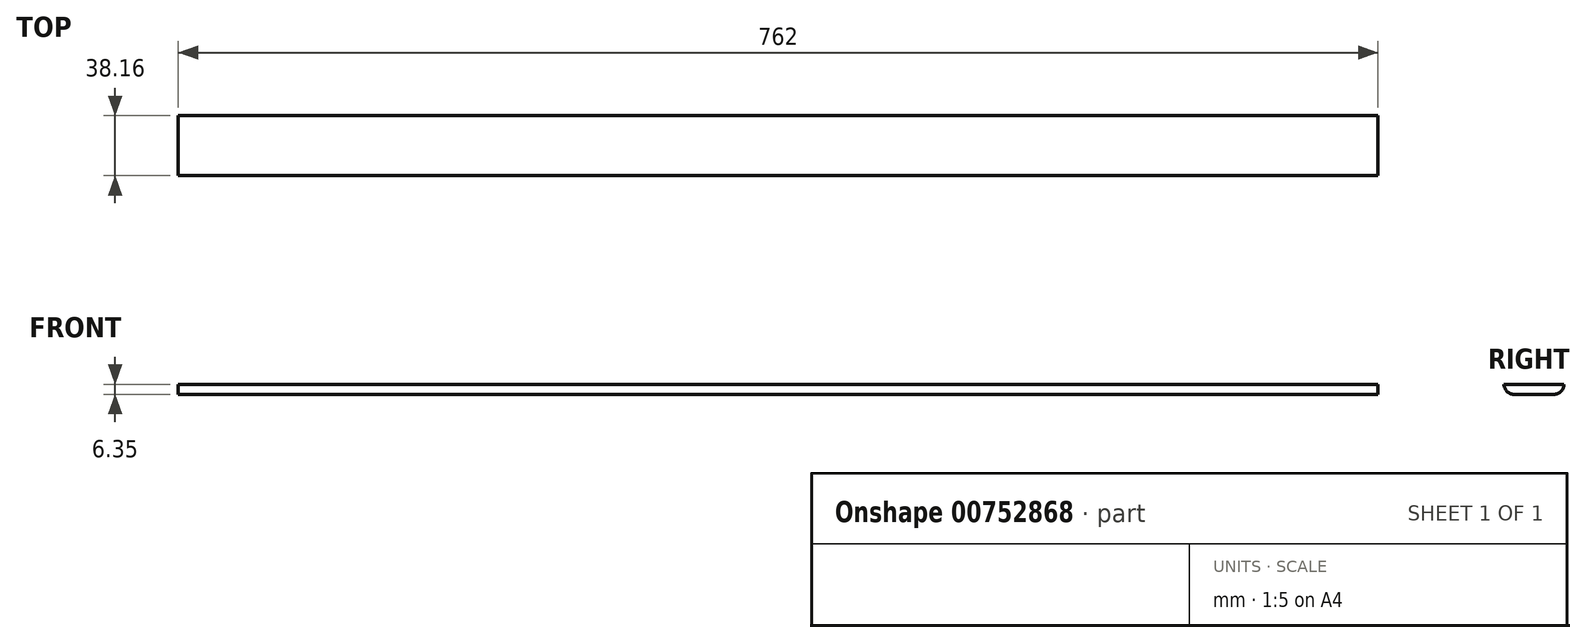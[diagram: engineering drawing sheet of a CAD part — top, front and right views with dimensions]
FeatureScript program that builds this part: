
annotation { "Feature Type Name" : "Feature", "Feature Type Description" : "" }
export const myFeature = defineFeature(function(context is Context, id is Id, definition is map)
    precondition{}
    {
        {
            var Q0;
            Q0=qCreatedBy(makeId("Right.planeOp"),FACE);
            var sketch = newSketch(context, id + "F0", { "sketchPlane" : qUnion([Q0])});
            skCircle(sketch, "E0", {"center": v(0, 2.7) * mm, "radius": 25 * mm});
            skCircle(sketch, "E1", {"center": v(0, 16.7) * mm, "radius": 11 * mm});
            skCircle(sketch, "E2", {"center": v(0, 16.7) * mm, "radius": 3.75 * mm});
            skLineSegment(sketch, "E3.bottom", {"start": v(12.73, 2.53) * mm, "end": v(-12.73, 2.53) * mm});
            skLineSegment(sketch, "E3.top", {"start": v(12.73, -10.17) * mm, "end": v(-12.73, -10.17) * mm});
            skLineSegment(sketch, "E3.left", {"start": v(19.08, -3.82) * mm, "end": v(19.08, -3.82) * mm});
            skLineSegment(sketch, "E3.right", {"start": v(-19.08, -3.82) * mm, "end": v(-19.08, -3.82) * mm});
            skPoint(sketch, "E3.middle", {"position": v(0, -3.82) * mm});
            skLineSegment(sketch, "E4", {"start": v(-19.08, -3.82) * mm, "end": v(19.08, -3.82) * mm});
            skPoint(sketch, "E5.visualSharp", {"position": v(-19.08, -10.17) * mm});
            skArc(sketch, "E5.filletArc", {"start": v(-19.08, -3.82) * mm, "mid": v(-17.22, -8.3) * mm, "end": v(-12.73, -10.17) * mm});
            skPoint(sketch, "E6.visualSharp", {"position": v(-19.08, 2.53) * mm});
            skArc(sketch, "E6.filletArc", {"start": v(-12.73, 2.53) * mm, "mid": v(-17.22, 0.67) * mm, "end": v(-19.08, -3.82) * mm});
            skPoint(sketch, "E7.visualSharp", {"position": v(19.08, 2.53) * mm});
            skArc(sketch, "E7.filletArc", {"start": v(19.08, -3.82) * mm, "mid": v(17.22, 0.67) * mm, "end": v(12.73, 2.53) * mm});
            skPoint(sketch, "E8.visualSharp", {"position": v(19.08, -10.17) * mm});
            skArc(sketch, "E8.filletArc", {"start": v(12.73, -10.17) * mm, "mid": v(17.22, -8.3) * mm, "end": v(19.08, -3.82) * mm});
            skLineSegment(sketch, "E9", {"start": v(-12.73, 2.53) * mm, "end": v(-3.23, 18.62) * mm});
            skLineSegment(sketch, "E10", {"start": v(12.73, 2.53) * mm, "end": v(3.23, 18.62) * mm});
            skLineSegment(sketch, "E11", {"start": v(0, 2.53) * mm, "end": v(0, -3.82) * mm});
            skLineSegment(sketch, "E12.bottom", {"start": v(-8.5, 2.53) * mm, "end": v(8.5, 2.53) * mm});
            skLineSegment(sketch, "E12.top", {"start": v(-8.5, -3.82) * mm, "end": v(8.5, -3.82) * mm});
            skLineSegment(sketch, "E12.left", {"start": v(-8.5, 2.53) * mm, "end": v(-8.5, -3.82) * mm});
            skLineSegment(sketch, "E12.right", {"start": v(8.5, 2.53) * mm, "end": v(8.5, -3.82) * mm});
            skPoint(sketch, "E12.middle", {"position": v(0, -0.64) * mm});
            skSolve(sketch);
        }
        {
            var Q0;
            Q0=makeQuery(id+"F0.imprint","IMPRINT",FACE,{"disambiguationData":[TD([[makeQuery(id+"F0.imprint","IMPRINT",EDGE,{"derivedFrom":sQuery(id+"F0.wireOp",EDGE,"E3.top")}),-1.0]])]});
            extrude(context, id + "F1", {"entities" : qUnion([Q0]), "depth" : 762 * mm, "offsetDistance" : 25.4 * mm});
        }
    });
